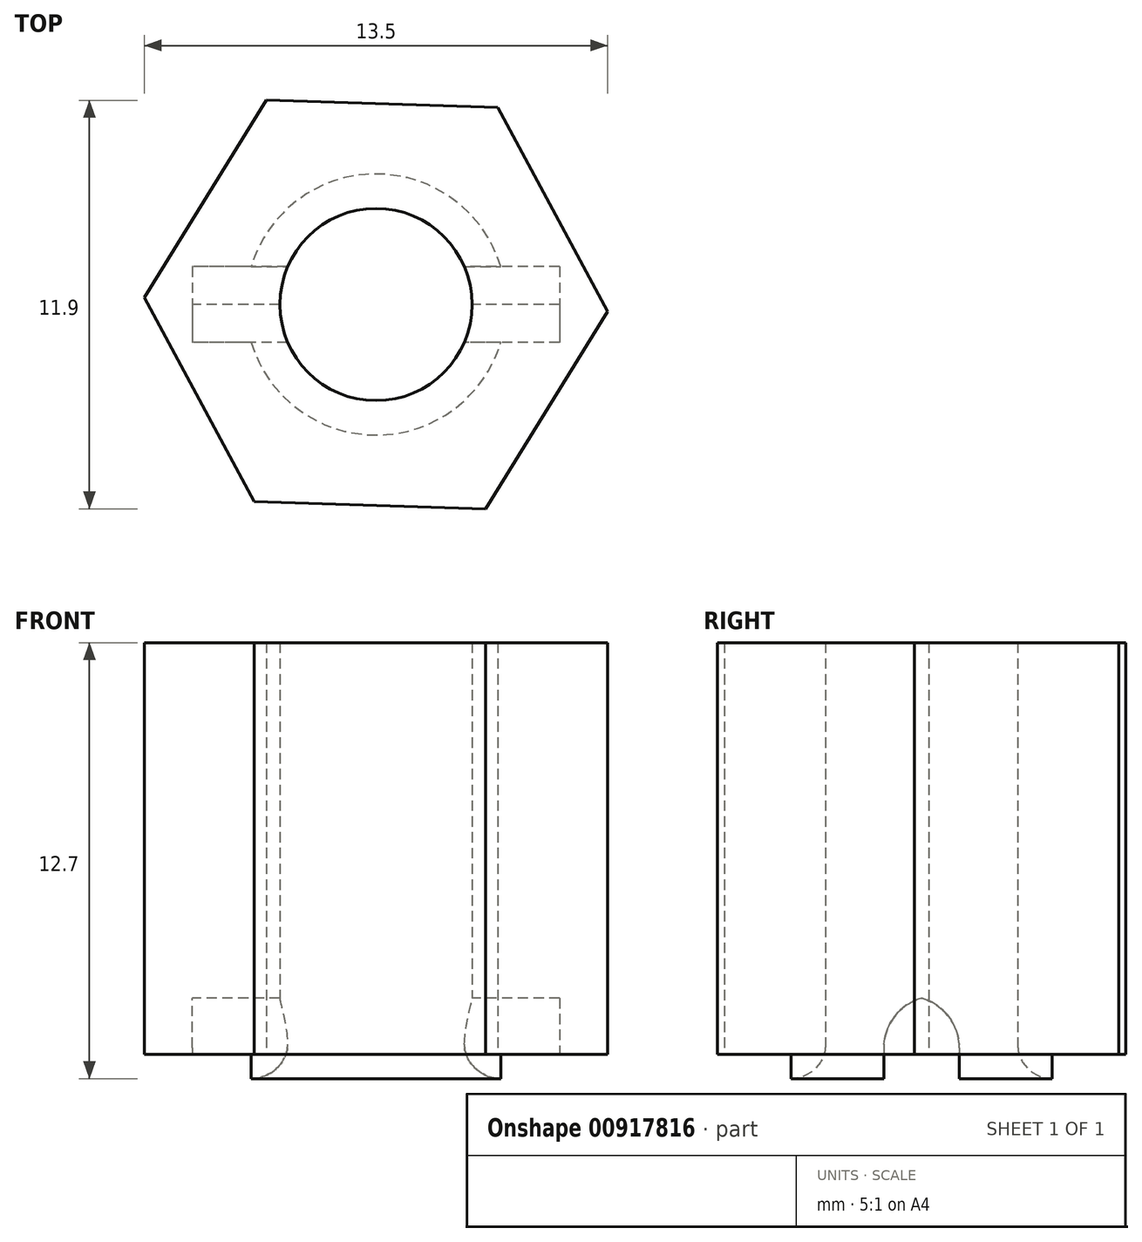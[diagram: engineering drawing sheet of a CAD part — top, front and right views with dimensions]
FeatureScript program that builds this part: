
annotation { "Feature Type Name" : "Feature", "Feature Type Description" : "" }
export const myFeature = defineFeature(function(context is Context, id is Id, definition is map)
    precondition{}
    {
        {
            var Q0;
            Q0=qCreatedBy(makeId("Top.planeOp"),FACE);
            var sketch = newSketch(context, id + "F0", { "sketchPlane" : qUnion([Q0])});
            skCircle(sketch, "E0.cCircle", {"center": v(0, 0) * mm, "radius": 5.85 * mm, "construction": true});
            skLineSegment(sketch, "E0.0", {"start": v(6.75, -0.2) * mm, "end": v(3.2, -5.95) * mm});
            skLineSegment(sketch, "E0.1", {"start": v(3.2, -5.95) * mm, "end": v(-3.55, -5.74) * mm});
            skLineSegment(sketch, "E0.2", {"start": v(-3.55, -5.74) * mm, "end": v(-6.75, 0.2) * mm});
            skLineSegment(sketch, "E0.3", {"start": v(-6.75, 0.2) * mm, "end": v(-3.2, 5.95) * mm});
            skLineSegment(sketch, "E0.4", {"start": v(-3.2, 5.95) * mm, "end": v(3.55, 5.74) * mm});
            skLineSegment(sketch, "E0.5", {"start": v(3.55, 5.74) * mm, "end": v(6.75, -0.2) * mm});
            skPoint(sketch, "E0.0.midPoint", {"position": v(4.97, -3.08) * mm});
            skCircle(sketch, "E1", {"center": v(0, 0) * mm, "radius": 2.8 * mm});
            skCircle(sketch, "E2", {"center": v(0, 0) * mm, "radius": 3.5 * mm});
            skSolve(sketch);
        }
        {
            var Q0;
            Q0=makeQuery(id+"F0.imprint","IMPRINT",FACE,{"disambiguationData":[TD([[makeQuery(id+"F0.imprint","IMPRINT",EDGE,{"derivedFrom":sQuery(id+"F0.wireOp",EDGE,"E0.0")}),-1.0]])]});
            var Q1;
            Q1=makeQuery(id+"F0.imprint","IMPRINT",FACE,{"disambiguationData":[TD([[makeQuery(id+"F0.imprint","IMPRINT",EDGE,{"derivedFrom":sQuery(id+"F0.wireOp",EDGE,"E1")}),-1.0]])]});
            extrude(context, id + "F1", {"entities" : qUnion([Q0, Q1]), "depth" : 12 * mm, "offsetDistance" : 25 * mm});
        }
        {
            var Q0;
            Q0=makeQuery(id+"F1.opExtrude","CAP_FACE",FACE,{"disambiguationData":[OSD([sQuery(id+"F0.wireOp",EDGE,"E0.0"),sQuery(id+"F0.wireOp",EDGE,"E0.1"),sQuery(id+"F0.wireOp",EDGE,"E0.2"),sQuery(id+"F0.wireOp",EDGE,"E0.3"),sQuery(id+"F0.wireOp",EDGE,"E0.4"),sQuery(id+"F0.wireOp",EDGE,"E0.5"),sQuery(id+"F0.wireOp",EDGE,"E1")])],"isStart":true});
            var sketch = newSketch(context, id + "F2", { "sketchPlane" : qUnion([Q0])});
            skLineSegment(sketch, "E3.bottom", {"start": v(5.35, -1.1) * mm, "end": v(-5.35, -1.1) * mm});
            skLineSegment(sketch, "E3.top", {"start": v(5.35, 1.1) * mm, "end": v(-5.35, 1.1) * mm});
            skLineSegment(sketch, "E3.left", {"start": v(5.35, -1.1) * mm, "end": v(5.35, 1.1) * mm});
            skLineSegment(sketch, "E3.right", {"start": v(-5.35, -1.1) * mm, "end": v(-5.35, 1.1) * mm});
            skSolve(sketch);
        }
        {
            var Q0;
            {var subQ0=sQuery(id+"F2.wireOp",EDGE,"E3.bottom");var subQ1=makeQuery(id+"F1.opExtrude","CAP_EDGE",EDGE,{"disambiguationData":[OSD([sQuery(id+"F0.wireOp",EDGE,"E1")])],"isStart":true});var subQ2=makeQuery(id+"F2.imprint","INTERSECT",VERTEX,{"disambiguationData":[OD(0.0)],"derivedFrom":[subQ1,subQ0]});Q0=makeQuery(id+"F2.imprint","IMPRINT",FACE,{"disambiguationData":[TD([[makeQuery(id+"F2.imprint","IMPRINT",EDGE,{"disambiguationData":[TD([[subQ2,-1.0]])],"derivedFrom":subQ0}),-1.0]])]});}
            var Q1;
            {var subQ0=sQuery(id+"F2.wireOp",EDGE,"E3.left");Q1=makeQuery(id+"F2.imprint","IMPRINT",FACE,{"disambiguationData":[TD([[makeQuery(id+"F2.imprint","IMPRINT",EDGE,{"derivedFrom":subQ0}),1.0]])]});}
            var Q2;
            {var subQ0=sQuery(id+"F2.wireOp",EDGE,"E3.right");Q2=makeQuery(id+"F2.imprint","IMPRINT",FACE,{"disambiguationData":[TD([[makeQuery(id+"F2.imprint","IMPRINT",EDGE,{"derivedFrom":subQ0}),-1.0]])]});}
            extrude(context, id + "F3", {"entities" : qUnion([Q0, Q1, Q2]), "operationType" : NewBodyOperationType.REMOVE, "oppositeDirection" : true, "depth" : 1.7 * mm, "offsetDistance" : 25 * mm});
        }
        {
            var Q0;
            {var subQ1=sQuery(id+"F2.wireOp",EDGE,"E3.left");Q0=makeQuery(id+"F2.imprint","IMPRINT",FACE,{"disambiguationData":[TD([[makeQuery(id+"F2.imprint","IMPRINT",EDGE,{"derivedFrom":subQ1}),-1.0]])]});}
            var Q1;
            {var subQ1=sQuery(id+"F2.wireOp",EDGE,"E3.left");Q1=makeQuery(id+"F2.imprint","IMPRINT",FACE,{"disambiguationData":[TD([[makeQuery(id+"F2.imprint","IMPRINT",EDGE,{"derivedFrom":subQ1}),-1.0]])]});}
            var sketch = newSketch(context, id + "F4", { "sketchPlane" : qUnion([Q0, Q1])});
            skCircle(sketch, "E4", {"center": v(0, 0) * mm, "radius": 3.8 * mm});
            skArc(sketch, "E5.0", {"start": v(2.57, -1.1) * mm, "mid": v(0, -2.8) * mm, "end": v(-2.57, -1.1) * mm});
            skLineSegment(sketch, "E6.0", {"start": v(5.35, -1.1) * mm, "end": v(-5.35, -1.1) * mm});
            skLineSegment(sketch, "E7.0", {"start": v(5.35, 1.1) * mm, "end": v(-5.35, 1.1) * mm});
            skPoint(sketch, "E8.0", {"position": v(5.35, 0) * mm});
            skLineSegment(sketch, "E9.0.0", {"start": v(-2.57, 1.1) * mm, "end": v(2.57, 1.1) * mm});
            skArc(sketch, "E9.0.1", {"start": v(2.57, 1.1) * mm, "mid": v(0, 2.8) * mm, "end": v(-2.57, 1.1) * mm});
            skLineSegment(sketch, "E10.0", {"start": v(-5.35, -1.1) * mm, "end": v(-5.35, 1.1) * mm});
            skSolve(sketch);
        }
        {
            var Q0;
            {var subQ4=sQuery(id+"F4.wireOp",EDGE,"E5.0");Q0=makeQuery(id+"F4.imprint","IMPRINT",FACE,{"disambiguationData":[TD([[makeQuery(id+"F4.imprint","IMPRINT",EDGE,{"derivedFrom":subQ4}),1.0]])]});}
            var Q1;
            {var subQ4=sQuery(id+"F4.wireOp",EDGE,"E9.0.1");Q1=makeQuery(id+"F4.imprint","IMPRINT",FACE,{"disambiguationData":[TD([[makeQuery(id+"F4.imprint","IMPRINT",EDGE,{"derivedFrom":subQ4}),1.0]])]});}
            extrude(context, id + "F5", {"entities" : qUnion([Q0, Q1]), "operationType" : NewBodyOperationType.ADD, "depth" : 0.7 * mm, "offsetDistance" : 25 * mm});
        }
        {
            var Q0;
            {var subQ0=sQuery(id+"F2.wireOp",EDGE,"E3.bottom");var subQ1=sQuery(id+"F2.wireOp",EDGE,"E3.left");Q0=makeQuery(id+"F3.boolean.opBoolean","COPY",EDGE,{"disambiguationData":[TD([makeQuery(id+"F3.opExtrude","SWEPT_FACE",FACE,{"disambiguationData":[OSD([subQ1])]})])],"derivedFrom":makeQuery(id+"F3.opExtrude","CAP_EDGE",EDGE,{"disambiguationData":[OSD([subQ0])],"isStart":false})});}
            var Q1;
            {var subQ0=sQuery(id+"F2.wireOp",EDGE,"E3.bottom");var subQ1=sQuery(id+"F2.wireOp",EDGE,"E3.right");Q1=makeQuery(id+"F3.boolean.opBoolean","COPY",EDGE,{"disambiguationData":[TD([makeQuery(id+"F3.opExtrude","SWEPT_FACE",FACE,{"disambiguationData":[OSD([subQ1])]})])],"derivedFrom":makeQuery(id+"F3.opExtrude","CAP_EDGE",EDGE,{"disambiguationData":[OSD([subQ0])],"isStart":false})});}
            var Q2;
            {var subQ0=sQuery(id+"F2.wireOp",EDGE,"E3.left");var subQ1=sQuery(id+"F2.wireOp",EDGE,"E3.top");Q2=makeQuery(id+"F3.boolean.opBoolean","COPY",EDGE,{"disambiguationData":[TD([makeQuery(id+"F3.opExtrude","SWEPT_FACE",FACE,{"disambiguationData":[OSD([subQ0])]})])],"derivedFrom":makeQuery(id+"F3.opExtrude","CAP_EDGE",EDGE,{"disambiguationData":[OSD([subQ1])],"isStart":false})});}
            var Q3;
            {var subQ0=sQuery(id+"F2.wireOp",EDGE,"E3.right");var subQ1=sQuery(id+"F2.wireOp",EDGE,"E3.top");Q3=makeQuery(id+"F3.boolean.opBoolean","COPY",EDGE,{"disambiguationData":[TD([makeQuery(id+"F3.opExtrude","SWEPT_FACE",FACE,{"disambiguationData":[OSD([subQ0])]})])],"derivedFrom":makeQuery(id+"F3.opExtrude","CAP_EDGE",EDGE,{"disambiguationData":[OSD([subQ1])],"isStart":false})});}
            fillet(context, id + "F6", {"entities" : qUnion([Q0, Q1, Q2, Q3]), "radius" : 1.5 * mm, "tangentPropagation" : true, "allowEdgeOverflow" : false});
        }
        {
            var Q0;
            Q0=makeQuery(id+"F5.opExtrude","CAP_EDGE",EDGE,{"disambiguationData":[OSD([sQuery(id+"F4.wireOp",EDGE,"E5.0")])],"isStart":false});
            var Q1;
            Q1=makeQuery(id+"F5.opExtrude","CAP_EDGE",EDGE,{"disambiguationData":[OSD([sQuery(id+"F4.wireOp",EDGE,"E9.0.1")])],"isStart":false});
            fillet(context, id + "F7", {"entities" : qUnion([Q0, Q1]), "radius" : 1 * mm, "tangentPropagation" : true, "allowEdgeOverflow" : false});
        }
    });
